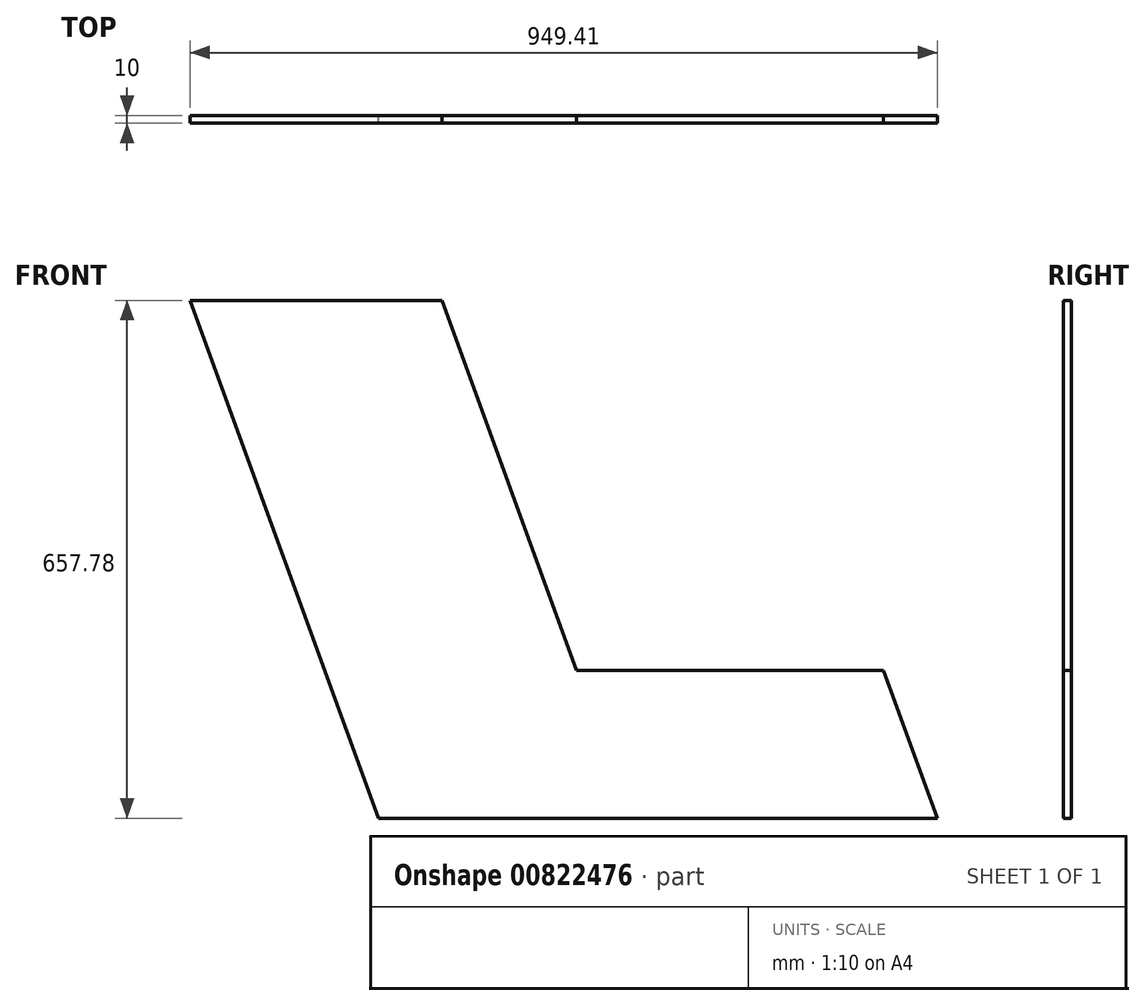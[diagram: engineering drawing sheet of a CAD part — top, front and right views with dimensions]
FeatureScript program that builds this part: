
annotation { "Feature Type Name" : "Feature", "Feature Type Description" : "" }
export const myFeature = defineFeature(function(context is Context, id is Id, definition is map)
    precondition{}
    {
        {
            var Q0;
            Q0=qCreatedBy(makeId("Front.planeOp"),FACE);
            var sketch = newSketch(context, id + "F0", { "sketchPlane" : qUnion([Q0])});
            skLineSegment(sketch, "E0", {"start": v(-517.24, -430.07) * mm, "end": v(192.76, -430.07) * mm});
            skLineSegment(sketch, "E1", {"start": v(124.36, -242.13) * mm, "end": v(-265.64, -242.13) * mm});
            skLineSegment(sketch, "E2", {"start": v(-265.64, -242.13) * mm, "end": v(-436.65, 227.71) * mm});
            skLineSegment(sketch, "E3", {"start": v(-436.65, 227.71) * mm, "end": v(-756.65, 227.71) * mm});
            skLineSegment(sketch, "E4", {"start": v(-756.65, 227.71) * mm, "end": v(-517.24, -430.07) * mm});
            skLineSegment(sketch, "E5", {"start": v(124.36, -242.13) * mm, "end": v(192.76, -430.07) * mm});
            skSolve(sketch);
        }
        {
            var Q0;
            Q0=makeQuery(id+"F0.imprint","IMPRINT",FACE,{"disambiguationData":[TD([[makeQuery(id+"F0.imprint","IMPRINT",EDGE,{"derivedFrom":sQuery(id+"F0.wireOp",EDGE,"E0")}),1.0]])]});
            var Q1;
            Q1=makeQuery(id+"F0.imprint","IMPRINT",FACE,{"disambiguationData":[TD([[makeQuery(id+"F0.imprint","IMPRINT",EDGE,{"derivedFrom":sQuery(id+"F0.wireOp",EDGE,"pgvErVKm-BDVy-IWiA-WicW-B6g0RcLyOcZ5")}),1.0]])]});
            extrude(context, id + "F1", {"entities" : qUnion([Q0, Q1]), "depth" : 10 * mm, "offsetDistance" : 25.4 * mm});
        }
    });
